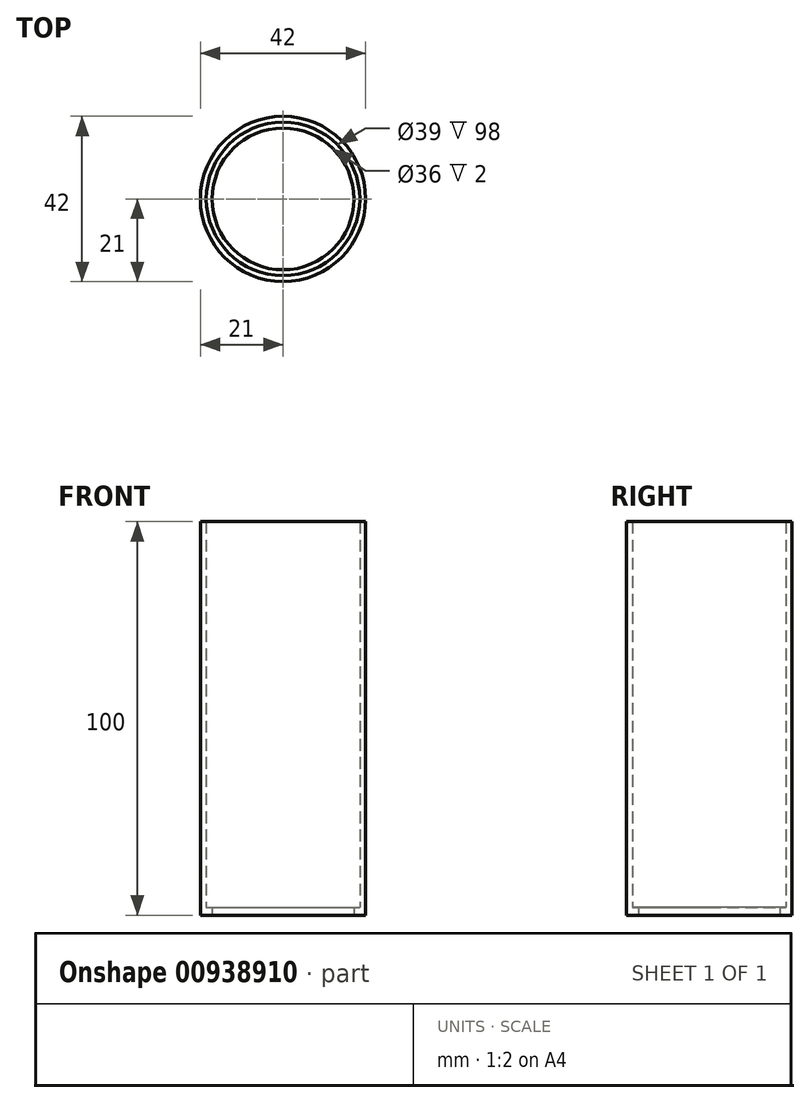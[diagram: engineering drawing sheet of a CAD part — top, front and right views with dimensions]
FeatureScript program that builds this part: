
annotation { "Feature Type Name" : "Feature", "Feature Type Description" : "" }
export const myFeature = defineFeature(function(context is Context, id is Id, definition is map)
    precondition{}
    {
        {
            var Q0;
            Q0=qCreatedBy(makeId("Top.planeOp"),FACE);
            var sketch = newSketch(context, id + "F0", { "sketchPlane" : qUnion([Q0])});
            skCircle(sketch, "E0", {"center": v(0, 0) * mm, "radius": 21 * mm});
            skCircle(sketch, "E1", {"center": v(0, 0) * mm, "radius": 19.5 * mm});
            skSolve(sketch);
        }
        {
            var Q0;
            Q0=qSketchRegion(id+"F0",true);
            extrude(context, id + "F1", {"entities" : qUnion([Q0]), "depth" : 100 * mm, "offsetDistance" : 25 * mm});
        }
        {
            var Q0;
            Q0=qCreatedBy(makeId("Right.planeOp"),FACE);
            var sketch = newSketch(context, id + "F2", { "sketchPlane" : qUnion([Q0])});
            skLineSegment(sketch, "E2.bottom", {"start": v(2, 4) * mm, "end": v(-2, 4) * mm});
            skLineSegment(sketch, "E2.top", {"start": v(2, 0) * mm, "end": v(-2, 0) * mm});
            skLineSegment(sketch, "E2.left", {"start": v(2, 4) * mm, "end": v(2, 0) * mm});
            skLineSegment(sketch, "E2.right", {"start": v(-2, 4) * mm, "end": v(-2, 0) * mm});
            skSolve(sketch);
        }
        {
            var Q0;
            Q0=makeQuery(id+"F1.opExtrude","CAP_FACE",FACE,{"disambiguationData":[OSD([sQuery(id+"F0.wireOp",EDGE,"E0"),sQuery(id+"F0.wireOp",EDGE,"E1")])],"isStart":true});
            var sketch = newSketch(context, id + "F3", { "sketchPlane" : qUnion([Q0])});
            skCircle(sketch, "E3", {"center": v(0, 0) * mm, "radius": 18 * mm});
            skCircle(sketch, "E4", {"center": v(0, 0) * mm, "radius": 21 * mm});
            skSolve(sketch);
        }
        {
            var Q0;
            Q0 = qSketchRegion(id + "F3", true);
            extrude(context, id + "F4", {"entities" : qUnion([Q0]), "operationType" : NewBodyOperationType.ADD, "oppositeDirection" : true, "depth" : 2 * mm, "offsetDistance" : 25 * mm});
        }
    });
